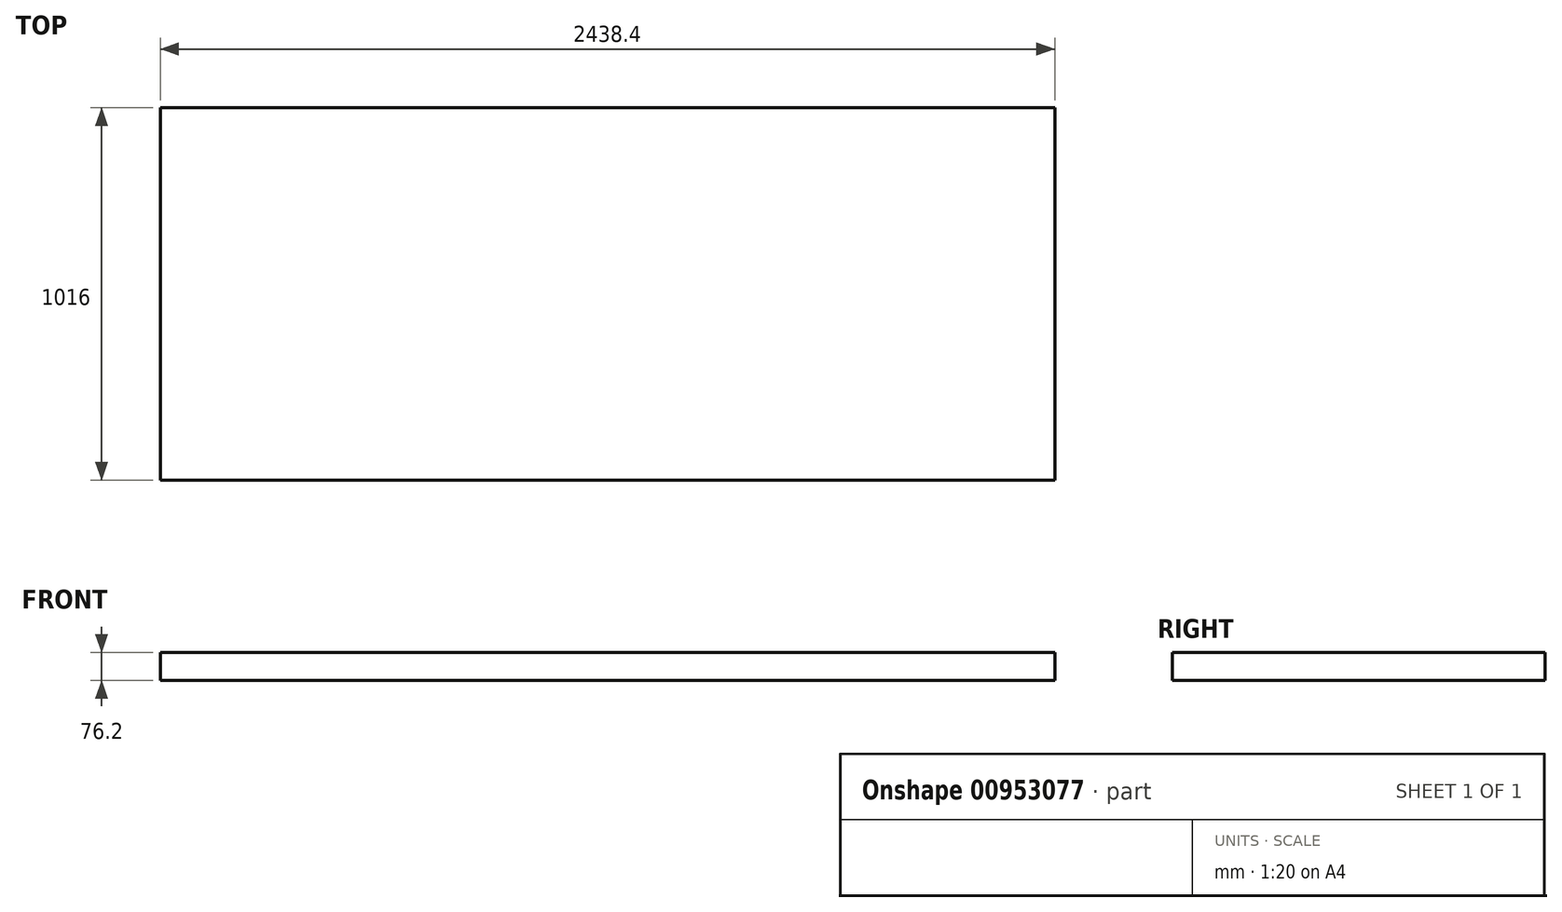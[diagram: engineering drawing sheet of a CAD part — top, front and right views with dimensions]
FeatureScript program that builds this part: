
annotation { "Feature Type Name" : "Feature", "Feature Type Description" : "" }
export const myFeature = defineFeature(function(context is Context, id is Id, definition is map)
    precondition{}
    {
        {
            var Q0;
            Q0=qCreatedBy(makeId("Top.planeOp"),FACE);
            var sketch = newSketch(context, id + "F0", { "sketchPlane" : qUnion([Q0])});
            skLineSegment(sketch, "E0", {"start": v(0, 0) * mm, "end": v(-2438.4, 0) * mm});
            skLineSegment(sketch, "E1", {"start": v(-2438.4, 0) * mm, "end": v(-2438.4, 1016) * mm});
            skLineSegment(sketch, "E2", {"start": v(-2438.4, 1016) * mm, "end": v(0, 1016) * mm});
            skLineSegment(sketch, "E3", {"start": v(0, 1016) * mm, "end": v(0, 0) * mm});
            skSolve(sketch);
        }
        {
            var Q0;
            Q0 = qSketchRegion(id + "F0", true);
            extrude(context, id + "F1", {"entities" : qUnion([Q0]), "depth" : 76.2 * mm, "offsetDistance" : 25.4 * mm});
        }
    });
